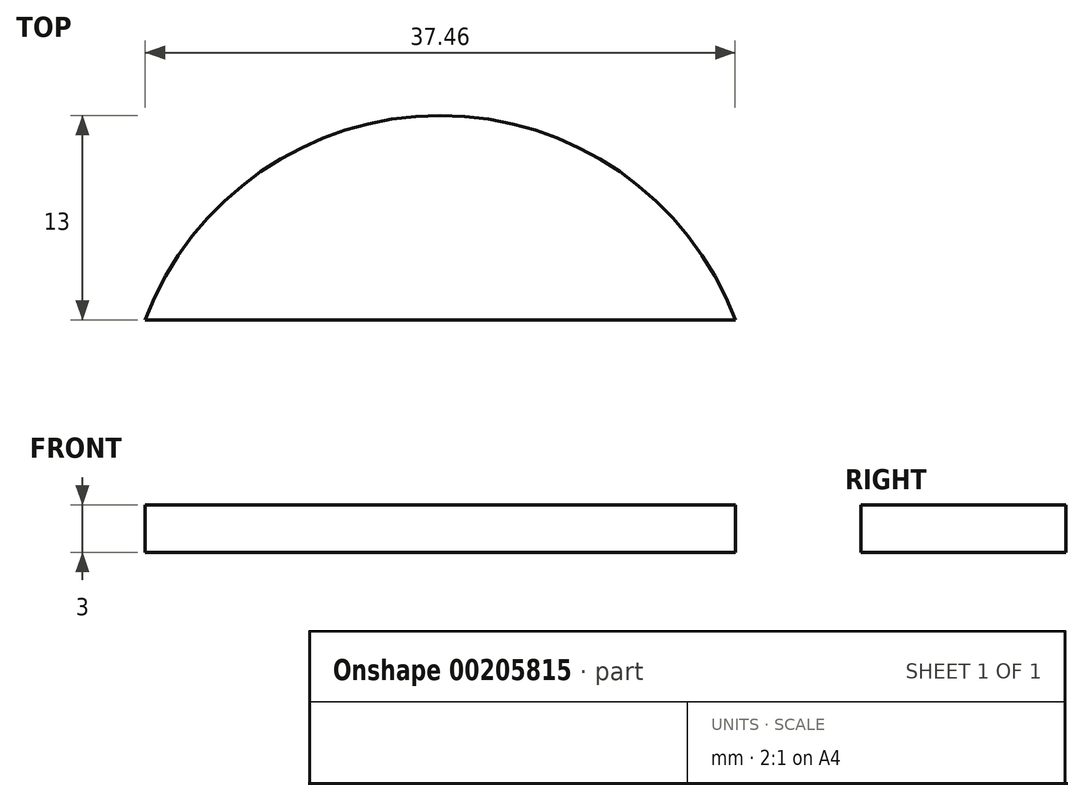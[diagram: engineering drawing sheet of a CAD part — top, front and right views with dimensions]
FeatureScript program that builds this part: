
annotation { "Feature Type Name" : "Feature", "Feature Type Description" : "" }
export const myFeature = defineFeature(function(context is Context, id is Id, definition is map)
    precondition{}
    {
        {
            var Q0;
            Q0=qCreatedBy(makeId("Top.planeOp"),FACE);
            var sketch = newSketch(context, id + "F0", { "sketchPlane" : qUnion([Q0])});
            skCircle(sketch, "E0", {"center": v(0, 0) * mm, "radius": 20 * mm});
            skLineSegment(sketch, "E1.bottom", {"start": v(26.23, -7) * mm, "end": v(-26.23, -7) * mm});
            skLineSegment(sketch, "E1.top", {"start": v(26.23, 7) * mm, "end": v(-26.23, 7) * mm});
            skLineSegment(sketch, "E1.left", {"start": v(26.23, -7) * mm, "end": v(26.23, 7) * mm});
            skLineSegment(sketch, "E1.right", {"start": v(-26.23, -7) * mm, "end": v(-26.23, 7) * mm});
            skSolve(sketch);
        }
        {
            var Q0;
            {var subQ0=sQuery(id+"F0.wireOp",EDGE,"E1.top");var subQ1=sQuery(id+"F0.wireOp",EDGE,"E0");var subQ2=makeQuery(id+"F0.imprint","INTERSECT",VERTEX,{"disambiguationData":[OD(0.0)],"derivedFrom":[subQ1,subQ0]});Q0=makeQuery(id+"F0.imprint","IMPRINT",FACE,{"disambiguationData":[TD([[makeQuery(id+"F0.imprint","IMPRINT",EDGE,{"disambiguationData":[TD([[subQ2,-1.0]])],"derivedFrom":subQ1}),1.0]])]});}
            extrude(context, id + "F1", {"entities" : qUnion([Q0]), "depth" : 3 * mm});
        }
        {
            var Q0;
            Q0=makeQuery(id+"F1.opExtrude","CAP_FACE",FACE,{"disambiguationData":[OSD([sQuery(id+"F0.wireOp",EDGE,"E0"),sQuery(id+"F0.wireOp",EDGE,"E1.bottom"),sQuery(id+"F0.wireOp",EDGE,"E1.top")])],"isStart":false});
            var sketch = newSketch(context, id + "F2", { "sketchPlane" : qUnion([Q0])});
            skPoint(sketch, "E2", {"position": v(-14, 0) * mm});
            skPoint(sketch, "E2.positionSnap0", {"position": v(-20, 0) * mm});
            skPoint(sketch, "E3.MirrorP", {"position": v(14, 0) * mm});
            skSolve(sketch);
        }
        {
            var Q0;
            Q0=sQuery(id+"F2.wireOp",VERTEX,"E2");
            var Q1;
            Q1=sQuery(id+"F2.wireOp",VERTEX,"E3.MirrorP");
            var Q2;
            Q2=makeQuery(id+"F1.opExtrude","SWEPT_BODY",BODY,{"disambiguationData":[OSD([sQuery(id+"F0.wireOp",EDGE,"E0"),sQuery(id+"F0.wireOp",EDGE,"E1.bottom"),sQuery(id+"F0.wireOp",EDGE,"E1.top")])]});
            hole(context, id + "F3", {"style" : HoleStyle.SIMPLE, "endStyle" : HoleEndStyle.THROUGH, "holeDiameter" : 6 * mm, "locations" : qUnion([Q0, Q1]), "scope" : qUnion([Q2]), "isTappedThrough" : true});
        }
    });
